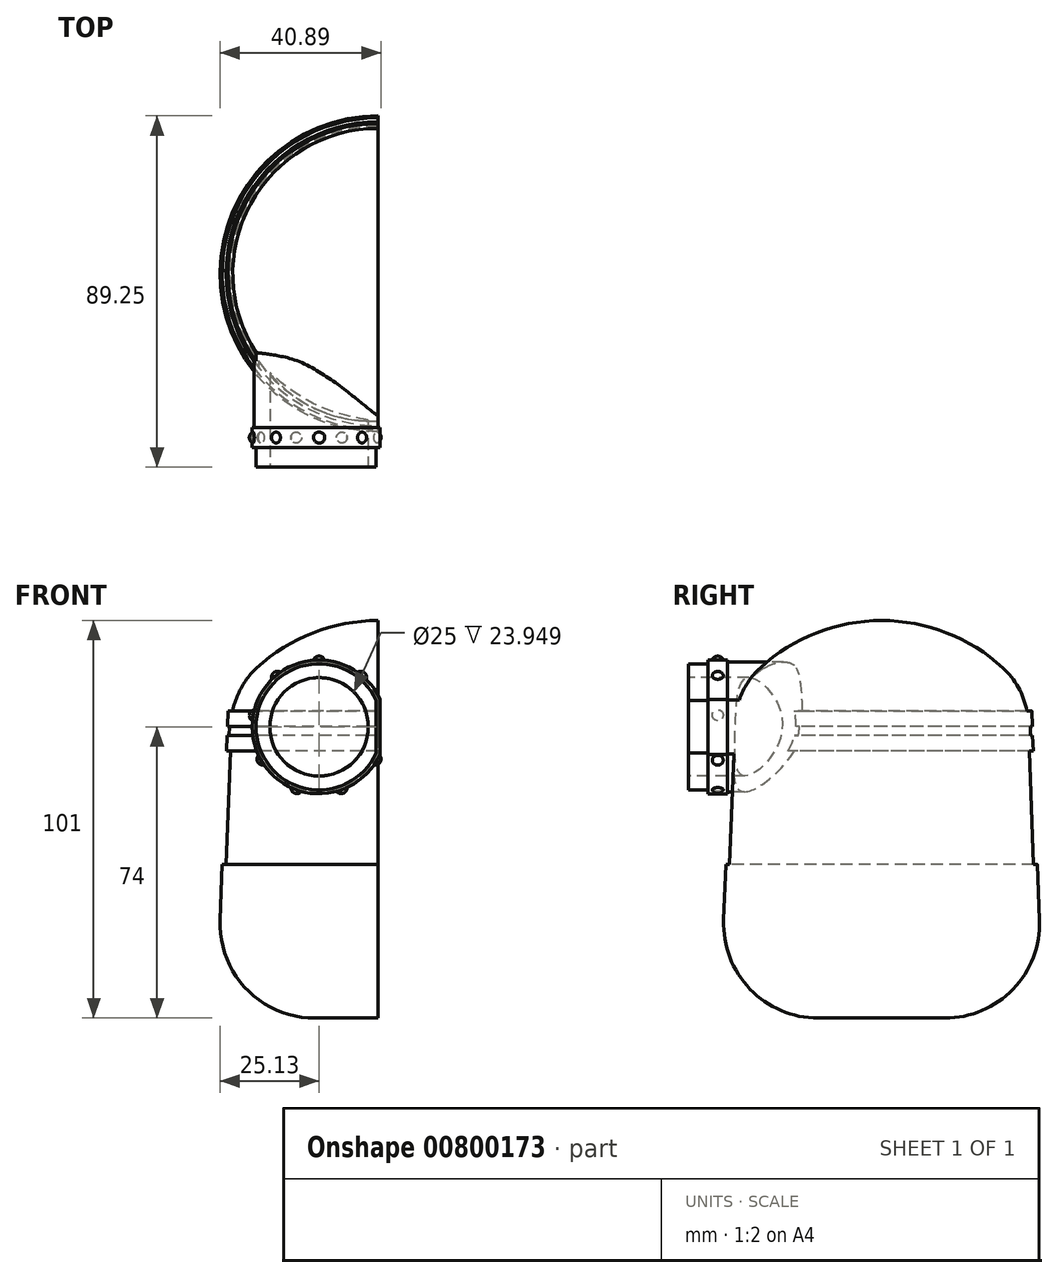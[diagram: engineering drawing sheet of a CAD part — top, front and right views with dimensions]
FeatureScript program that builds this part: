
annotation { "Feature Type Name" : "Feature", "Feature Type Description" : "" }
export const myFeature = defineFeature(function(context is Context, id is Id, definition is map)
    precondition{}
    {
        {
            var Q0;
            Q0=qCreatedBy(makeId("Right.planeOp"),FACE);
            var sketch = newSketch(context, id + "F0", { "sketchPlane" : qUnion([Q0])});
            skLineSegment(sketch, "E0", {"start": v(0, 0) * mm, "end": v(0, -100) * mm});
            skLineSegment(sketch, "E1", {"start": v(0, -100) * mm, "end": v(-16.13, -100) * mm});
            skLineSegment(sketch, "E2", {"start": v(-39.12, -76.15) * mm, "end": v(-37.26, -26) * mm});
            skLineSegment(sketch, "E3", {"start": v(0, 0) * mm, "end": v(87.48, 0) * mm, "construction": true});
            skArc(sketch, "E4", {"start": v(0, 0) * mm, "mid": v(-16.53, -3.1) * mm, "end": v(-30.8, -12) * mm});
            skPoint(sketch, "E5.visualSharp", {"position": v(-40, -100) * mm});
            skArc(sketch, "E5.filletArc", {"start": v(-39.12, -76.15) * mm, "mid": v(-32.7, -92.96) * mm, "end": v(-16.13, -100) * mm});
            skPoint(sketch, "E6.visualSharp", {"position": v(-37, -19) * mm});
            skArc(sketch, "E6.filletArc", {"start": v(-30.8, -12) * mm, "mid": v(-35.43, -18.35) * mm, "end": v(-37.26, -26) * mm});
            skSolve(sketch);
        }
        {
            var Q0;
            Q0=makeQuery(id+"F0.imprint","IMPRINT",FACE,{"disambiguationData":[TD([[makeQuery(id+"F0.imprint","IMPRINT",EDGE,{"derivedFrom":sQuery(id+"F0.wireOp",EDGE,"E0")}),-1.0]])]});
            var Q1;
            Q1=sQuery(id+"F0.wireOp",EDGE,"E0");
            revolve(context, id + "F1", {"surfaceOperationType" : NewSurfaceOperationType.NEW, "entities" : qUnion([Q0]), "axis" : qUnion([Q1]), "revolveType" : RevolveType.ONE_DIRECTION, "angle" : 180 * degree});
        }
        {
            var Q0;
            Q0=qCreatedBy(makeId("Front.planeOp"),FACE);
            var Q1;
            Q1=makeQuery(id+"F1.opRevolve","CAP_VERTEX",VERTEX,{"disambiguationData":[OSD([sQuery(id+"F0.wireOp",EDGE,"E2"),sQuery(id+"F0.wireOp",EDGE,"E5.filletArc")])],"isStart":true});
            cPlane(context, id + "F2", {"entities" : qUnion([Q0, Q1]), "cplaneType" : CPlaneType.PLANE_POINT, "offset" : 25 * mm, "width" : 150 * mm, "height" : 150 * mm});
        }
        {
            var Q0;
            Q0=qCreatedBy(id+"F2.planeOp",FACE);
            var sketch = newSketch(context, id + "F3", { "sketchPlane" : qUnion([Q0])});
            skArc(sketch, "E7", {"start": v(0, -20.13) * mm, "mid": v(-31.5, -27) * mm, "end": v(0, -33.87) * mm});
            skLineSegment(sketch, "E8", {"start": v(0, -20.13) * mm, "end": v(0, -33.87) * mm});
            skSolve(sketch);
        }
        {
            var Q0;
            Q0 = qSketchRegion(id + "F3", true);
            var Q1;
            Q1=makeQuery(id+"F1.opRevolve","SWEPT_FACE",FACE,{"disambiguationData":[OSD([sQuery(id+"F0.wireOp",EDGE,"E6.filletArc")])]});
            extrude(context, id + "F4", {"entities" : qUnion([Q0]), "operationType" : NewBodyOperationType.ADD, "endBound" : BoundingType.UP_TO_SURFACE, "oppositeDirection" : true, "depth" : 25 * mm, "endBoundEntityFace" : qUnion([Q1]), "offsetDistance" : 25 * mm});
        }
        {
            var Q0;
            Q0=makeQuery(id+"F4.opExtrude","CAP_FACE",FACE,{"disambiguationData":[OSD([sQuery(id+"F3.wireOp",EDGE,"E7"),sQuery(id+"F3.wireOp",EDGE,"E8")])],"isStart":true});
            var sketch = newSketch(context, id + "F5", { "sketchPlane" : qUnion([Q0])});
            skLineSegment(sketch, "E9.0", {"start": v(0.5, -33.98) * mm, "end": v(0.5, -20.02) * mm});
            skArc(sketch, "E9.1", {"start": v(0.5, -20.02) * mm, "mid": v(-32, -27) * mm, "end": v(0.5, -33.98) * mm});
            skSolve(sketch);
        }
        {
            var Q0;
            Q0 = qSketchRegion(id + "F5", true);
            extrude(context, id + "F6", {"entities" : qUnion([Q0]), "operationType" : NewBodyOperationType.ADD, "depth" : 5 * mm, "offsetDistance" : 25 * mm});
        }
        {
            var Q0;
            Q0=makeQuery(id+"F0.imprint","IMPRINT",FACE,{"disambiguationData":[TD([[makeQuery(id+"F0.imprint","IMPRINT",EDGE,{"derivedFrom":sQuery(id+"F0.wireOp",EDGE,"E0")}),-1.0]])]});
            var sketch = newSketch(context, id + "F7", { "sketchPlane" : qUnion([Q0])});
            skLineSegment(sketch, "E10", {"start": v(35.45, -27.96) * mm, "end": v(-20.38, -27.96) * mm, "construction": true});
            skLineSegment(sketch, "E11", {"start": v(35.45, -27.96) * mm, "end": v(47.71, -27.96) * mm, "construction": true});
            skLineSegment(sketch, "E12", {"start": v(38.14, -22.94) * mm, "end": v(38.29, -26.94) * mm});
            skLineSegment(sketch, "E13", {"start": v(38.29, -26.94) * mm, "end": v(37.8, -26.96) * mm});
            skLineSegment(sketch, "E14", {"start": v(38.14, -22.94) * mm, "end": v(36.64, -23) * mm});
            skLineSegment(sketch, "E15", {"start": v(38.37, -29.16) * mm, "end": v(38.52, -33.1) * mm});
            skLineSegment(sketch, "E16", {"start": v(37.83, -29.14) * mm, "end": v(38.37, -29.16) * mm});
            skLineSegment(sketch, "E17", {"start": v(38.52, -33.1) * mm, "end": v(37.24, -33.14) * mm});
            skLineSegment(sketch, "E18", {"start": v(36.64, -23) * mm, "end": v(37.24, -33.14) * mm});
            skLineSegment(sketch, "E19", {"start": v(37.8, -26.96) * mm, "end": v(37.83, -29.14) * mm});
            skSolve(sketch);
        }
        {
            var Q0;
            Q0=sQuery(id+"F7.wireOp",EDGE,"E12");
            cPoint(context, id + "F8", {"entities" : qUnion([Q0]), "parameter" : 0.5});
        }
        {
            var Q0;
            Q0=qCreatedBy(makeId("Top.planeOp"),FACE);
            var Q1;
            Q1 = qCreatedBy(id + "F8" ,VERTEX);
            cPlane(context, id + "F9", {"entities" : qUnion([Q0, Q1]), "cplaneType" : CPlaneType.PLANE_POINT, "offset" : 25 * mm, "width" : 150 * mm, "height" : 150 * mm});
        }
        {
            var Q0;
            Q0=qCreatedBy(id+"F9.planeOp",FACE);
            var sketch = newSketch(context, id + "F10", { "sketchPlane" : qUnion([Q0])});
            skArc(sketch, "E20", {"start": v(0, 37) * mm, "mid": v(-35.65, 9.9) * mm, "end": v(-19.08, -31.7) * mm});
            skSolve(sketch);
        }
        {
            var Q0;
            Q0 = qSketchRegion(id + "F7", true);
            var Q1;
            Q1 = qConstructionFilter(qBodyType(qCreatedBy(id + "F10" ,EDGE), BodyType.WIRE), ConstructionObject.NO);
            sweep(context, id + "F11", {"operationType" : NewBodyOperationType.ADD, "profiles" : qUnion([Q0]), "path" : qUnion([Q1])});
        }
        {
            var Q0;
            Q0=makeQuery(id+"F6.opExtrude","CAP_FACE",FACE,{"disambiguationData":[OSD([sQuery(id+"F5.wireOp",EDGE,"E9.0"),sQuery(id+"F5.wireOp",EDGE,"E9.1")])],"isStart":false});
            var sketch = newSketch(context, id + "F12", { "sketchPlane" : qUnion([Q0])});
            skArc(sketch, "E21.0", {"start": v(-0.45, -20.33) * mm, "mid": v(-31, -27) * mm, "end": v(-0.45, -33.67) * mm});
            skLineSegment(sketch, "E22", {"start": v(-0.45, -33.67) * mm, "end": v(-0.45, -20.33) * mm});
            skSolve(sketch);
        }
        {
            var Q0;
            Q0 = qSketchRegion(id + "F12", true);
            extrude(context, id + "F13", {"entities" : qUnion([Q0]), "operationType" : NewBodyOperationType.ADD, "depth" : 5 * mm, "offsetDistance" : 25 * mm});
        }
        {
            var Q0;
            Q0=qCreatedBy(id+"F2.planeOp",FACE);
            cPlane(context, id + "F14", {"entities" : qUnion([Q0]), "cplaneType" : CPlaneType.OFFSET, "offset" : 2.5 * mm, "width" : 150 * mm, "height" : 150 * mm});
        }
        {
            var Q0;
            Q0=qCreatedBy(id+"F14.planeOp",FACE);
            var sketch = newSketch(context, id + "F15", { "sketchPlane" : qUnion([Q0])});
            skLineSegment(sketch, "E23", {"start": v(-15, -27) * mm, "end": v(-15, -5.76) * mm, "construction": true});
            skArc(sketch, "E24", {"start": v(-15, -9.03) * mm, "mid": v(-16.06, -9.47) * mm, "end": v(-16.5, -10.53) * mm});
            skLineSegment(sketch, "E25", {"start": v(-15, -10.53) * mm, "end": v(-16.5, -10.53) * mm, "construction": true});
            skLineSegment(sketch, "E26", {"start": v(-16.5, -10.53) * mm, "end": v(-15, -10.53) * mm});
            skLineSegment(sketch, "E27", {"start": v(-15, -10.53) * mm, "end": v(-15, -9.03) * mm});
            skLineSegment(sketch, "E28", {"start": v(-15, -27) * mm, "end": v(3.39, -23.76) * mm, "construction": true});
            skLineSegment(sketch, "E29", {"start": v(-25.58, -14.39) * mm, "end": v(-26.55, -13.24) * mm});
            skLineSegment(sketch, "E30", {"start": v(-25.58, -14.39) * mm, "end": v(-26.73, -15.35) * mm});
            skArc(sketch, "E31", {"start": v(-26.55, -13.24) * mm, "mid": v(-27.08, -14.26) * mm, "end": v(-26.73, -15.35) * mm});
            skLineSegment(sketch, "E32", {"start": v(-31.22, -24.14) * mm, "end": v(-31.48, -25.62) * mm});
            skArc(sketch, "E33", {"start": v(-32.7, -23.88) * mm, "mid": v(-32.44, -25) * mm, "end": v(-31.48, -25.62) * mm});
            skLineSegment(sketch, "E34", {"start": v(-31.22, -24.14) * mm, "end": v(-32.7, -23.88) * mm});
            skLineSegment(sketch, "E35", {"start": v(-4.42, -14.39) * mm, "end": v(-5.56, -13.42) * mm});
            skArc(sketch, "E36", {"start": v(-3.45, -13.24) * mm, "mid": v(-4.55, -12.9) * mm, "end": v(-5.56, -13.42) * mm});
            skLineSegment(sketch, "E37", {"start": v(-4.42, -14.39) * mm, "end": v(-3.45, -13.24) * mm});
            skLineSegment(sketch, "E38", {"start": v(-29.26, -35.23) * mm, "end": v(-28.5, -36.53) * mm});
            skArc(sketch, "E39", {"start": v(-30.56, -35.98) * mm, "mid": v(-29.65, -36.68) * mm, "end": v(-28.5, -36.53) * mm});
            skLineSegment(sketch, "E40", {"start": v(-29.26, -35.23) * mm, "end": v(-30.56, -35.98) * mm});
            skLineSegment(sketch, "E41", {"start": v(-20.63, -42.47) * mm, "end": v(-19.22, -42.99) * mm});
            skArc(sketch, "E42", {"start": v(-21.14, -43.88) * mm, "mid": v(-20, -43.83) * mm, "end": v(-19.22, -42.99) * mm});
            skLineSegment(sketch, "E43", {"start": v(-20.63, -42.47) * mm, "end": v(-21.14, -43.88) * mm});
            skLineSegment(sketch, "E44", {"start": v(-9.37, -42.47) * mm, "end": v(-7.96, -41.96) * mm});
            skArc(sketch, "E45", {"start": v(-8.86, -43.88) * mm, "mid": v(-8, -43.1) * mm, "end": v(-7.96, -41.96) * mm});
            skLineSegment(sketch, "E46", {"start": v(-9.37, -42.47) * mm, "end": v(-8.86, -43.88) * mm});
            skLineSegment(sketch, "E47", {"start": v(-0.74, -35.23) * mm, "end": v(0, -33.93) * mm});
            skArc(sketch, "E48", {"start": v(0.56, -35.98) * mm, "mid": v(0.7, -34.84) * mm, "end": v(0, -33.93) * mm});
            skLineSegment(sketch, "E49", {"start": v(-0.74, -35.23) * mm, "end": v(0.56, -35.98) * mm});
            skSolve(sketch);
        }
        {
            var Q0;
            Q0=makeQuery(id+"F15.imprint","IMPRINT",FACE,{"disambiguationData":[TD([[makeQuery(id+"F15.imprint","IMPRINT",EDGE,{"derivedFrom":sQuery(id+"F15.wireOp",EDGE,"E24")}),1.0]])]});
            var Q1;
            Q1=sQuery(id+"F15.wireOp",EDGE,"E23");
            revolve(context, id + "F16", {"operationType" : NewBodyOperationType.ADD, "surfaceOperationType" : NewSurfaceOperationType.NEW, "entities" : qUnion([Q0]), "axis" : qUnion([Q1]), "revolveType" : RevolveType.FULL});
        }
        {
            var Q0;
            Q0=makeQuery(id+"F15.imprint","IMPRINT",FACE,{"disambiguationData":[TD([[makeQuery(id+"F15.imprint","IMPRINT",EDGE,{"derivedFrom":sQuery(id+"F15.wireOp",EDGE,"E29")}),1.0]])]});
            var Q1;
            Q1=sQuery(id+"F15.wireOp",EDGE,"E29");
            revolve(context, id + "F17", {"operationType" : NewBodyOperationType.ADD, "surfaceOperationType" : NewSurfaceOperationType.NEW, "entities" : qUnion([Q0]), "axis" : qUnion([Q1]), "revolveType" : RevolveType.FULL});
        }
        {
            var Q0;
            Q0=makeQuery(id+"F15.imprint","IMPRINT",FACE,{"disambiguationData":[TD([[makeQuery(id+"F15.imprint","IMPRINT",EDGE,{"derivedFrom":sQuery(id+"F15.wireOp",EDGE,"E32")}),-1.0]])]});
            var Q1;
            Q1=sQuery(id+"F15.wireOp",EDGE,"E34");
            revolve(context, id + "F18", {"operationType" : NewBodyOperationType.ADD, "surfaceOperationType" : NewSurfaceOperationType.NEW, "entities" : qUnion([Q0]), "axis" : qUnion([Q1]), "revolveType" : RevolveType.FULL});
        }
        {
            var Q0;
            Q0=makeQuery(id+"F15.imprint","IMPRINT",FACE,{"disambiguationData":[TD([[makeQuery(id+"F15.imprint","IMPRINT",EDGE,{"derivedFrom":sQuery(id+"F15.wireOp",EDGE,"E38")}),-1.0]])]});
            var Q1;
            Q1=sQuery(id+"F15.wireOp",EDGE,"E40");
            revolve(context, id + "F19", {"operationType" : NewBodyOperationType.ADD, "surfaceOperationType" : NewSurfaceOperationType.NEW, "entities" : qUnion([Q0]), "axis" : qUnion([Q1]), "revolveType" : RevolveType.FULL});
        }
        {
            var Q0;
            Q0=makeQuery(id+"F15.imprint","IMPRINT",FACE,{"disambiguationData":[TD([[makeQuery(id+"F15.imprint","IMPRINT",EDGE,{"derivedFrom":sQuery(id+"F15.wireOp",EDGE,"E41")}),-1.0]])]});
            var Q1;
            Q1=sQuery(id+"F15.wireOp",EDGE,"E43");
            revolve(context, id + "F20", {"operationType" : NewBodyOperationType.ADD, "surfaceOperationType" : NewSurfaceOperationType.NEW, "entities" : qUnion([Q0]), "axis" : qUnion([Q1]), "revolveType" : RevolveType.FULL});
        }
        {
            var Q0;
            Q0=makeQuery(id+"F15.imprint","IMPRINT",FACE,{"disambiguationData":[TD([[makeQuery(id+"F15.imprint","IMPRINT",EDGE,{"derivedFrom":sQuery(id+"F15.wireOp",EDGE,"E44")}),-1.0]])]});
            var Q1;
            Q1=sQuery(id+"F15.wireOp",EDGE,"E46");
            revolve(context, id + "F21", {"operationType" : NewBodyOperationType.ADD, "surfaceOperationType" : NewSurfaceOperationType.NEW, "entities" : qUnion([Q0]), "axis" : qUnion([Q1]), "revolveType" : RevolveType.FULL});
        }
        {
            var Q0;
            Q0=makeQuery(id+"F15.imprint","IMPRINT",FACE,{"disambiguationData":[TD([[makeQuery(id+"F15.imprint","IMPRINT",EDGE,{"derivedFrom":sQuery(id+"F15.wireOp",EDGE,"E35")}),-1.0]])]});
            var Q1;
            Q1=sQuery(id+"F15.wireOp",EDGE,"E37");
            revolve(context, id + "F22", {"operationType" : NewBodyOperationType.ADD, "surfaceOperationType" : NewSurfaceOperationType.NEW, "entities" : qUnion([Q0]), "axis" : qUnion([Q1]), "revolveType" : RevolveType.FULL});
        }
        {
            var Q0;
            Q0=makeQuery(id+"F15.imprint","IMPRINT",FACE,{"disambiguationData":[TD([[makeQuery(id+"F15.imprint","IMPRINT",EDGE,{"derivedFrom":sQuery(id+"F15.wireOp",EDGE,"E47")}),-1.0]])]});
            var Q1;
            Q1=sQuery(id+"F15.wireOp",EDGE,"E49");
            revolve(context, id + "F23", {"operationType" : NewBodyOperationType.ADD, "surfaceOperationType" : NewSurfaceOperationType.NEW, "entities" : qUnion([Q0]), "axis" : qUnion([Q1]), "revolveType" : RevolveType.FULL});
        }
        {
            var Q0;
            Q0=makeQuery(id+"F11.boolean.opBoolean","MERGE",FACE,{"derivedFrom":[makeQuery(id+"F4.boolean.opBoolean","MERGE",FACE,{"derivedFrom":[makeQuery(id+"F1.opRevolve","CAP_FACE",FACE,{"disambiguationData":[OSD([sQuery(id+"F0.wireOp",EDGE,"E0"),sQuery(id+"F0.wireOp",EDGE,"E1"),sQuery(id+"F0.wireOp",EDGE,"E2"),sQuery(id+"F0.wireOp",EDGE,"E4"),sQuery(id+"F0.wireOp",EDGE,"E5.filletArc"),sQuery(id+"F0.wireOp",EDGE,"E6.filletArc")])],"isStart":true}),makeQuery(id+"F4.opExtrude","SWEPT_FACE",FACE,{"disambiguationData":[OSD([sQuery(id+"F3.wireOp",EDGE,"E8")])]})]}),makeQuery(id+"F11.opSweep","CAP_FACE",FACE,{"disambiguationData":[OSD([sQuery(id+"F7.wireOp",EDGE,"E12"),sQuery(id+"F7.wireOp",EDGE,"E13"),sQuery(id+"F7.wireOp",EDGE,"E14"),sQuery(id+"F7.wireOp",EDGE,"E15"),sQuery(id+"F7.wireOp",EDGE,"E16"),sQuery(id+"F7.wireOp",EDGE,"E17"),sQuery(id+"F7.wireOp",EDGE,"E18"),sQuery(id+"F7.wireOp",EDGE,"E19"),sQuery(id+"F10.wireOp",VERTEX,"E20.start")])],"isStart":true})]});
            var sketch = newSketch(context, id + "F24", { "sketchPlane" : qUnion([Q0])});
            skArc(sketch, "E50.0", {"start": v(-40.12, -76.11) * mm, "mid": v(-33.41, -93.65) * mm, "end": v(-16.13, -101) * mm});
            skLineSegment(sketch, "E51.0", {"start": v(-40.12, -76.11) * mm, "end": v(-39.6, -62) * mm});
            skLineSegment(sketch, "E52.0", {"start": v(0, -101) * mm, "end": v(-16.13, -101) * mm});
            skLineSegment(sketch, "E53", {"start": v(-39.6, -62) * mm, "end": v(-38.33, -62) * mm});
            skPoint(sketch, "E53.startSnap0", {"position": v(-38.33, -62) * mm});
            skPoint(sketch, "E54.orphan", {"position": v(-44.68, -62) * mm});
            skLineSegment(sketch, "E55.0", {"start": v(-39.12, -76.15) * mm, "end": v(-37.26, -26) * mm});
            skArc(sketch, "E56.0", {"start": v(-39.12, -76.15) * mm, "mid": v(-32.7, -92.96) * mm, "end": v(-16.13, -100) * mm});
            skLineSegment(sketch, "E57.0", {"start": v(0, -100) * mm, "end": v(-16.13, -100) * mm});
            skLineSegment(sketch, "E58", {"start": v(0, -100) * mm, "end": v(0, -101) * mm});
            skPoint(sketch, "E59.orphan", {"position": v(-4.45, -62) * mm});
            skPoint(sketch, "E60.orphan", {"position": v(0, -87.12) * mm});
            skSolve(sketch);
        }
        {
            var Q0;
            Q0 = qSketchRegion(id + "F24", true);
            var Q1;
            Q1=sQuery(id+"F0.wireOp",EDGE,"E0");
            revolve(context, id + "F25", {"operationType" : NewBodyOperationType.ADD, "surfaceOperationType" : NewSurfaceOperationType.NEW, "entities" : qUnion([Q0]), "axis" : qUnion([Q1]), "revolveType" : RevolveType.ONE_DIRECTION, "angle" : 180 * degree});
        }
        {
            var Q0;
            Q0=makeQuery(id+"F0.imprint","IMPRINT",FACE,{"disambiguationData":[TD([[makeQuery(id+"F0.imprint","IMPRINT",EDGE,{"derivedFrom":sQuery(id+"F0.wireOp",EDGE,"E0")}),-1.0]])]});
            cPlane(context, id + "F26", {"entities" : qUnion([Q0]), "cplaneType" : CPlaneType.OFFSET, "offset" : 42 * mm, "oppositeDirection" : true, "width" : 150 * mm, "height" : 150 * mm});
        }
        {
            var Q0;
            Q0=qCreatedBy(id+"F26.planeOp",FACE);
            var sketch = newSketch(context, id + "F27", { "sketchPlane" : qUnion([Q0])});
            skLineSegment(sketch, "E61.bottom", {"start": v(30, -43.03) * mm, "end": v(-30, -43.03) * mm});
            skLineSegment(sketch, "E61.top", {"start": v(30, -74) * mm, "end": v(-30, -74) * mm});
            skLineSegment(sketch, "E61.left", {"start": v(30, -43.03) * mm, "end": v(30, -74) * mm});
            skLineSegment(sketch, "E61.right", {"start": v(-30, -43.03) * mm, "end": v(-30, -74) * mm});
            skPoint(sketch, "E61.middle", {"position": v(0, -58.51) * mm});
            skSolve(sketch);
        }
        {
            var Q0;
            Q0 = qSketchRegion(id + "F27", true);
            var Q1;
            Q1=makeQuery(id+"F25.opRevolve","SWEPT_FACE",FACE,{"disambiguationData":[OSD([sQuery(id+"F24.wireOp",EDGE,"E51.0")])]});
            extrude(context, id + "F28", {"entities" : qUnion([Q0]), "operationType" : NewBodyOperationType.REMOVE, "endBound" : BoundingType.UP_TO_SURFACE, "depth" : 25 * mm, "endBoundEntityFace" : qUnion([Q1]), "offsetDistance" : 25 * mm});
        }
        {
            var Q0;
            Q0=makeQuery(id+"F13.opExtrude","CAP_FACE",FACE,{"disambiguationData":[OSD([sQuery(id+"F12.wireOp",EDGE,"E21.0"),sQuery(id+"F12.wireOp",EDGE,"E22")])],"isStart":false});
            var sketch = newSketch(context, id + "F29", { "sketchPlane" : qUnion([Q0])});
            skCircle(sketch, "E62", {"center": v(-15, -27) * mm, "radius": 12.5 * mm});
            skSolve(sketch);
        }
        {
            var Q0;
            Q0 = qSketchRegion(id + "F29", true);
            var Q1;
            Q1=makeQuery(id+"F1.opRevolve","SWEPT_FACE",FACE,{"disambiguationData":[OSD([sQuery(id+"F0.wireOp",EDGE,"E2")])]});
            extrude(context, id + "F30", {"entities" : qUnion([Q0]), "operationType" : NewBodyOperationType.REMOVE, "endBound" : BoundingType.UP_TO_SURFACE, "oppositeDirection" : true, "depth" : 7 * mm, "endBoundEntityFace" : qUnion([Q1]), "offsetDistance" : 25 * mm});
        }
    });
